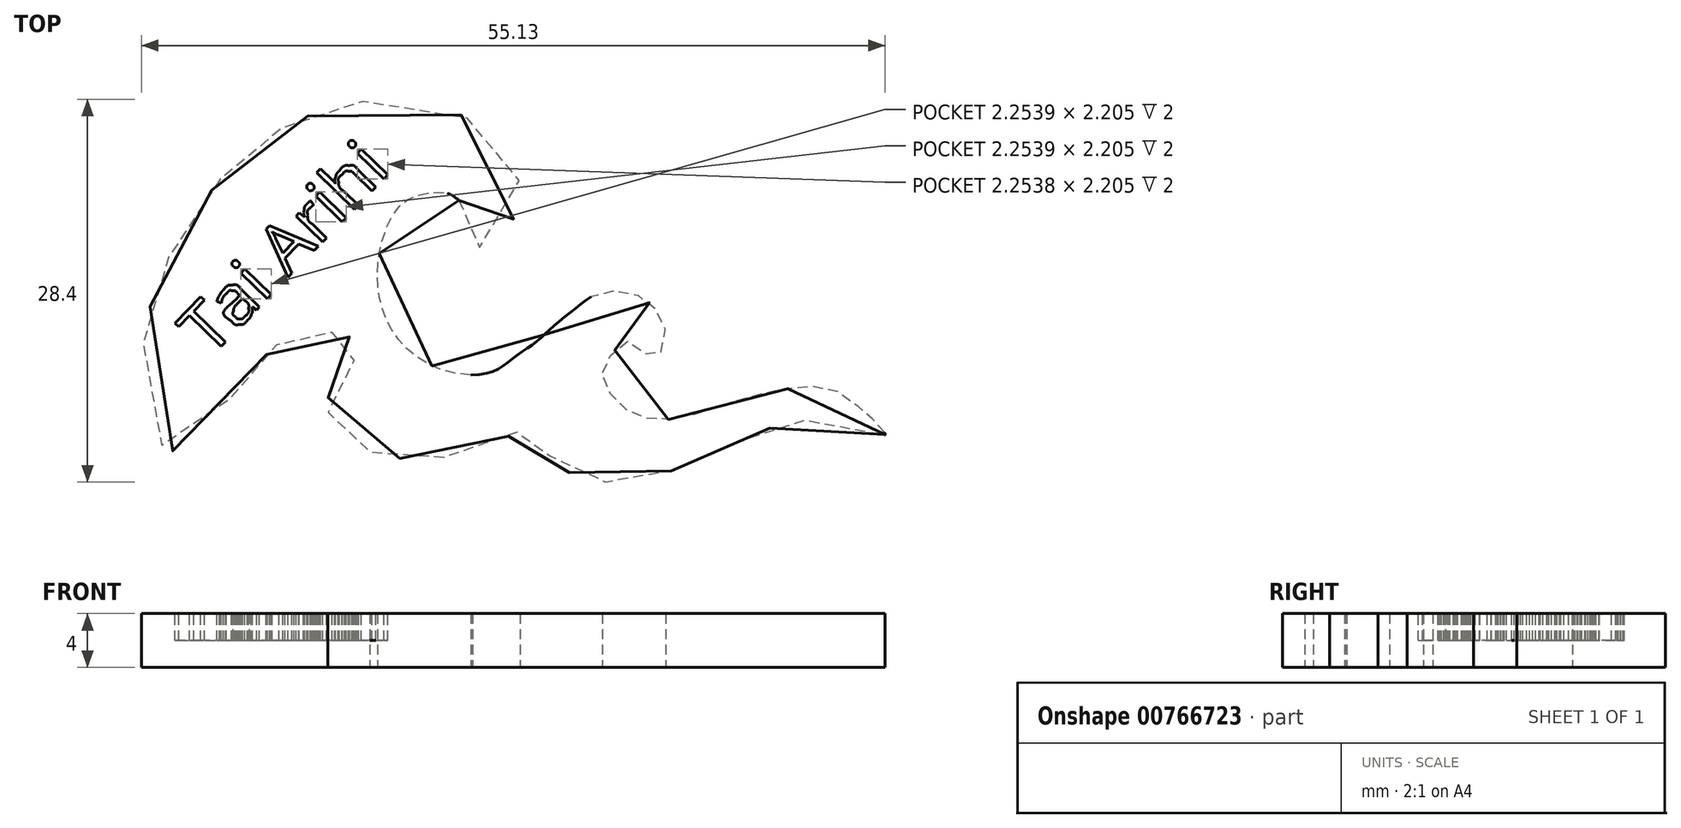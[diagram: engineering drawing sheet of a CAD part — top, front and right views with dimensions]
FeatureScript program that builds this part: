
annotation { "Feature Type Name" : "Feature", "Feature Type Description" : "" }
export const myFeature = defineFeature(function(context is Context, id is Id, definition is map)
    precondition{}
    {
        {
            var Q0;
            Q0=qCreatedBy(makeId("Top.planeOp"),FACE);
            var sketch = newSketch(context, id + "F0", { "sketchPlane" : qUnion([Q0])});
            skFitSpline(sketch, "E0", {"points": [v(-4, 7.32) * mm, v(-3.17, 6.5) * mm, v(-3.03, 5.12) * mm, v(-2.94, 3.88) * mm, v(-1.05, 4.57) * mm, v(0.33, 6.63) * mm, v(0.33, 9.3) * mm, v(-1.1, 11.33) * mm, v(-2.75, 13.03) * mm, v(-6.71, 14.6) * mm, v(-10.83, 14.7) * mm, v(-14.26, 13.9) * mm, v(-16.5, 13.04) * mm, v(-17.87, 12.21) * mm, v(-19.38, 11.18) * mm, v(-21.73, 8.83) * mm, v(-23.82, 6) * mm, v(-25.4, 3.36) * mm, v(-26.4, 0.65) * mm, v(-27.01, -0.9) * mm, v(-27.41, -7.48) * mm, v(-26.41, -10.04) * mm, v(-25.48, -11.27) * mm, v(-22.14, -9.08) * mm, v(-20.52, -6.72) * mm, v(-19, -4.9) * mm, v(-17.96, -3.83) * mm, v(-17.16, -3.15) * mm, v(-16.24, -2.8) * mm, v(-15.12, -2.5) * mm, v(-13.56, -2.45) * mm, v(-12.02, -2.86) * mm, v(-10.62, -4.24) * mm, v(-11.44, -4.4) * mm, v(-12.26, -5) * mm, v(-13.12, -5.94) * mm, v(-13.62, -6.85) * mm, v(-13.57, -8.97) * mm, v(-12.9, -10.01) * mm, v(-12.3, -10.65) * mm, v(-10.6, -11.34) * mm, v(-8, -11.86) * mm, v(-6.26, -11.88) * mm, v(-4.58, -11.65) * mm, v(-2.42, -11.25) * mm, v(-0.35, -10.18) * mm, v(1.58, -9.17) * mm, v(2, -8.82) * mm, v(2.24, -10.21) * mm, v(3.33, -12.42) * mm, v(4.27, -12.9) * mm, v(5.5, -13.34) * mm, v(7.56, -13.58) * mm, v(9.57, -13.4) * mm, v(11.07, -12.99) * mm, v(12.95, -12.28) * mm, v(15.2, -11.35) * mm, v(16.49, -10.68) * mm, v(17.86, -10.04) * mm, v(19.28, -9.48) * mm, v(21.13, -9.02) * mm, v(23.5, -9.09) * mm, v(26.74, -9.8) * mm, v(27.6, -10.05) * mm, v(26.97, -9.18) * mm, v(26.03, -8.38) * mm, v(24.07, -6.86) * mm, v(21.2, -6.54) * mm, v(18.35, -7.06) * mm, v(16.12, -7.7) * mm, v(14.1, -8.35) * mm, v(11.77, -8.9) * mm, v(9.35, -8.7) * mm, v(7.72, -7.6) * mm, v(6.64, -5.8) * mm, v(7.22, -4.21) * mm, v(8.76, -3.15) * mm, v(10.37, -4.33) * mm, v(11.3, -3.09) * mm, v(10.8, -1.06) * mm, v(9.3, 0.25) * mm, v(6.64, 0.5) * mm, v(4.87, -0.5) * mm, v(2.87, -2.14) * mm, v(1.58, -3.3) * mm, v(0, -4.4) * mm, v(-1.57, -5.4) * mm, v(-5, -5.34) * mm, v(-8.07, -3.46) * mm, v(-9.55, -1.09) * mm, v(-10.04, 1.33) * mm, v(-9.8, 3.94) * mm, v(-8.5, 6.8) * mm, v(-6.73, 7.79) * mm, v(-4.84, 7.84) * mm, v(-4, 7.32) * mm]});
            skSolve(sketch);
        }
        {
            var Q0;
            Q0 = qSketchRegion(id + "F0", true);
            extrude(context, id + "F1", {"entities" : qUnion([Q0]), "depth" : 4 * mm, "offsetDistance" : 25 * mm});
        }
        {
            var Q0;
            Q0=makeQuery(id+"F1.opExtrude","CAP_FACE",FACE,{"disambiguationData":[OSD([sQuery(id+"F0.wireOp",EDGE,"E0")])],"isStart":false});
            var sketch = newSketch(context, id + "F2", { "sketchPlane" : qUnion([Q0])});
            skLineSegment(sketch, "E1.0.0", {"start": v(-19, -0.8) * mm, "end": v(-18.79, -0.58) * mm});
            skLineSegment(sketch, "E1.0.1", {"start": v(-18.79, -0.58) * mm, "end": v(-20.13, 0.72) * mm});
            skFitSpline(sketch, "E1.0.2", {"points": [v(-20.13, 0.72) * mm, v(-20.47, 1.05) * mm, v(-20.8, 1.04) * mm]});
            skFitSpline(sketch, "E1.0.3", {"points": [v(-20.8, 1.04) * mm, v(-21.11, 1.02) * mm, v(-21.45, 0.67) * mm]});
            skFitSpline(sketch, "E1.0.4", {"points": [v(-21.45, 0.67) * mm, v(-21.62, 0.5) * mm, v(-21.75, 0.27) * mm]});
            skFitSpline(sketch, "E1.0.5", {"points": [v(-21.75, 0.27) * mm, v(-21.87, 0.06) * mm, v(-21.93, -0.16) * mm]});
            skLineSegment(sketch, "E1.0.6", {"start": v(-21.93, -0.16) * mm, "end": v(-21.62, -0.3) * mm});
            skFitSpline(sketch, "E1.0.7", {"points": [v(-21.62, -0.3) * mm, v(-21.47, 0.16) * mm, v(-21.23, 0.4) * mm]});
            skFitSpline(sketch, "E1.0.8", {"points": [v(-21.23, 0.4) * mm, v(-21.01, 0.63) * mm, v(-20.8, 0.62) * mm]});
            skFitSpline(sketch, "E1.0.9", {"points": [v(-20.8, 0.62) * mm, v(-20.6, 0.61) * mm, v(-20.37, 0.39) * mm]});
            skLineSegment(sketch, "E1.0.10", {"start": v(-20.37, 0.39) * mm, "end": v(-20.25, 0.27) * mm});
            skLineSegment(sketch, "E1.0.11", {"start": v(-20.25, 0.27) * mm, "end": v(-20.56, -0.07) * mm});
            skFitSpline(sketch, "E1.0.12", {"points": [v(-20.56, -0.07) * mm, v(-21.46, -1.05) * mm, v(-20.86, -1.63) * mm]});
            skFitSpline(sketch, "E1.0.13", {"points": [v(-20.86, -1.63) * mm, v(-20.58, -1.9) * mm, v(-20.27, -1.88) * mm]});
            skFitSpline(sketch, "E1.0.14", {"points": [v(-20.27, -1.88) * mm, v(-19.96, -1.86) * mm, v(-19.68, -1.57) * mm]});
            skFitSpline(sketch, "E1.0.15", {"points": [v(-19.68, -1.57) * mm, v(-19.46, -1.35) * mm, v(-19.39, -1.14) * mm]});
            skFitSpline(sketch, "E1.0.16", {"points": [v(-19.39, -1.14) * mm, v(-19.31, -0.93) * mm, v(-19.35, -0.6) * mm]});
            skLineSegment(sketch, "E1.0.17", {"start": v(-19.35, -0.6) * mm, "end": v(-19.34, -0.6) * mm});
            skLineSegment(sketch, "E1.0.18", {"start": v(-19.34, -0.6) * mm, "end": v(-19, -0.8) * mm});
            skLineSegment(sketch, "E2.0.0", {"start": v(-21.32, -3.2) * mm, "end": v(-23.67, -0.91) * mm});
            skLineSegment(sketch, "E2.0.1", {"start": v(-23.67, -0.91) * mm, "end": v(-22.86, -0.08) * mm});
            skLineSegment(sketch, "E2.0.2", {"start": v(-22.86, -0.08) * mm, "end": v(-23.14, 0.18) * mm});
            skLineSegment(sketch, "E2.0.3", {"start": v(-23.14, 0.18) * mm, "end": v(-25.04, -1.78) * mm});
            skLineSegment(sketch, "E2.0.4", {"start": v(-25.04, -1.78) * mm, "end": v(-24.77, -2.04) * mm});
            skLineSegment(sketch, "E2.0.5", {"start": v(-24.77, -2.04) * mm, "end": v(-23.97, -1.21) * mm});
            skLineSegment(sketch, "E2.0.6", {"start": v(-23.97, -1.21) * mm, "end": v(-21.62, -3.5) * mm});
            skLineSegment(sketch, "E2.0.7", {"start": v(-21.62, -3.5) * mm, "end": v(-21.32, -3.2) * mm});
            skFitSpline(sketch, "E3.0.0", {"points": [v(-20.71, 2.43) * mm, v(-20.61, 2.33) * mm, v(-20.52, 2.33) * mm]});
            skFitSpline(sketch, "E3.0.1", {"points": [v(-20.52, 2.33) * mm, v(-20.42, 2.34) * mm, v(-20.34, 2.41) * mm]});
            skFitSpline(sketch, "E3.0.2", {"points": [v(-20.34, 2.41) * mm, v(-20.28, 2.48) * mm, v(-20.27, 2.58) * mm]});
            skFitSpline(sketch, "E3.0.3", {"points": [v(-20.27, 2.58) * mm, v(-20.27, 2.68) * mm, v(-20.37, 2.78) * mm]});
            skFitSpline(sketch, "E3.0.4", {"points": [v(-20.37, 2.78) * mm, v(-20.47, 2.88) * mm, v(-20.57, 2.87) * mm]});
            skFitSpline(sketch, "E3.0.5", {"points": [v(-20.57, 2.87) * mm, v(-20.67, 2.87) * mm, v(-20.74, 2.8) * mm]});
            skFitSpline(sketch, "E3.0.6", {"points": [v(-20.74, 2.8) * mm, v(-20.81, 2.72) * mm, v(-20.82, 2.62) * mm]});
            skFitSpline(sketch, "E3.0.7", {"points": [v(-20.82, 2.62) * mm, v(-20.82, 2.53) * mm, v(-20.71, 2.43) * mm]});
            skLineSegment(sketch, "E4.0.0", {"start": v(-17.9, 0.33) * mm, "end": v(-19.87, 2.24) * mm});
            skLineSegment(sketch, "E4.0.1", {"start": v(-19.87, 2.24) * mm, "end": v(-20.16, 1.94) * mm});
            skLineSegment(sketch, "E4.0.2", {"start": v(-20.16, 1.94) * mm, "end": v(-18.2, 0.03) * mm});
            skLineSegment(sketch, "E4.0.3", {"start": v(-18.2, 0.03) * mm, "end": v(-17.9, 0.33) * mm});
            skLineSegment(sketch, "E5.0.0", {"start": v(-14.72, 3.6) * mm, "end": v(-14.42, 3.92) * mm});
            skLineSegment(sketch, "E5.0.1", {"start": v(-14.42, 3.92) * mm, "end": v(-18.05, 5.44) * mm});
            skLineSegment(sketch, "E5.0.2", {"start": v(-18.05, 5.44) * mm, "end": v(-18.3, 5.19) * mm});
            skLineSegment(sketch, "E5.0.3", {"start": v(-18.3, 5.19) * mm, "end": v(-16.67, 1.6) * mm});
            skLineSegment(sketch, "E5.0.4", {"start": v(-16.67, 1.6) * mm, "end": v(-16.37, 1.9) * mm});
            skLineSegment(sketch, "E5.0.5", {"start": v(-16.37, 1.9) * mm, "end": v(-16.9, 3.04) * mm});
            skLineSegment(sketch, "E5.0.6", {"start": v(-16.9, 3.04) * mm, "end": v(-15.87, 4.09) * mm});
            skLineSegment(sketch, "E5.0.7", {"start": v(-15.87, 4.09) * mm, "end": v(-14.72, 3.6) * mm});
            skFitSpline(sketch, "E6.0.0", {"points": [v(-15.24, 7.08) * mm, v(-15.42, 6.9) * mm, v(-15.47, 6.64) * mm]});
            skFitSpline(sketch, "E6.0.1", {"points": [v(-15.47, 6.64) * mm, v(-15.51, 6.38) * mm, v(-15.43, 6.08) * mm]});
            skLineSegment(sketch, "E6.0.2", {"start": v(-15.43, 6.08) * mm, "end": v(-15.44, 6.07) * mm});
            skLineSegment(sketch, "E6.0.3", {"start": v(-15.44, 6.07) * mm, "end": v(-15.84, 6.39) * mm});
            skLineSegment(sketch, "E6.0.4", {"start": v(-15.84, 6.39) * mm, "end": v(-16.07, 6.14) * mm});
            skLineSegment(sketch, "E6.0.5", {"start": v(-16.07, 6.14) * mm, "end": v(-14.11, 4.24) * mm});
            skLineSegment(sketch, "E6.0.6", {"start": v(-14.11, 4.24) * mm, "end": v(-13.82, 4.53) * mm});
            skLineSegment(sketch, "E6.0.7", {"start": v(-13.82, 4.53) * mm, "end": v(-14.88, 5.56) * mm});
            skFitSpline(sketch, "E6.0.8", {"points": [v(-14.88, 5.56) * mm, v(-15.16, 5.84) * mm, v(-15.2, 6.2) * mm]});
            skFitSpline(sketch, "E6.0.9", {"points": [v(-15.2, 6.2) * mm, v(-15.22, 6.55) * mm, v(-15, 6.8) * mm]});
            skFitSpline(sketch, "E6.0.10", {"points": [v(-15, 6.8) * mm, v(-14.9, 6.88) * mm, v(-14.76, 6.98) * mm]});
            skLineSegment(sketch, "E6.0.11", {"start": v(-14.76, 6.98) * mm, "end": v(-15, 7.29) * mm});
            skFitSpline(sketch, "E6.0.12", {"points": [v(-15, 7.29) * mm, v(-15.11, 7.2) * mm, v(-15.24, 7.08) * mm]});
            skLineSegment(sketch, "E7.0.0", {"start": v(-12.37, 6.03) * mm, "end": v(-14.33, 7.94) * mm});
            skLineSegment(sketch, "E7.0.1", {"start": v(-14.33, 7.94) * mm, "end": v(-14.62, 7.64) * mm});
            skLineSegment(sketch, "E7.0.2", {"start": v(-14.62, 7.64) * mm, "end": v(-12.66, 5.74) * mm});
            skLineSegment(sketch, "E7.0.3", {"start": v(-12.66, 5.74) * mm, "end": v(-12.37, 6.03) * mm});
            skFitSpline(sketch, "E8.0.0", {"points": [v(-15.18, 8.13) * mm, v(-15.08, 8.04) * mm, v(-14.98, 8.04) * mm]});
            skFitSpline(sketch, "E8.0.1", {"points": [v(-14.98, 8.04) * mm, v(-14.88, 8.04) * mm, v(-14.8, 8.12) * mm]});
            skFitSpline(sketch, "E8.0.2", {"points": [v(-14.8, 8.12) * mm, v(-14.74, 8.19) * mm, v(-14.74, 8.29) * mm]});
            skFitSpline(sketch, "E8.0.3", {"points": [v(-14.74, 8.29) * mm, v(-14.74, 8.39) * mm, v(-14.84, 8.49) * mm]});
            skFitSpline(sketch, "E8.0.4", {"points": [v(-14.84, 8.49) * mm, v(-14.94, 8.58) * mm, v(-15.03, 8.58) * mm]});
            skFitSpline(sketch, "E8.0.5", {"points": [v(-15.03, 8.58) * mm, v(-15.13, 8.57) * mm, v(-15.2, 8.5) * mm]});
            skFitSpline(sketch, "E8.0.6", {"points": [v(-15.2, 8.5) * mm, v(-15.28, 8.43) * mm, v(-15.28, 8.33) * mm]});
            skFitSpline(sketch, "E8.0.7", {"points": [v(-15.28, 8.33) * mm, v(-15.28, 8.23) * mm, v(-15.18, 8.13) * mm]});
            skLineSegment(sketch, "E9.0.0", {"start": v(-10.45, 8) * mm, "end": v(-10.16, 8.3) * mm});
            skLineSegment(sketch, "E9.0.1", {"start": v(-10.16, 8.3) * mm, "end": v(-11.44, 9.55) * mm});
            skFitSpline(sketch, "E9.0.2", {"points": [v(-11.44, 9.55) * mm, v(-11.81, 9.91) * mm, v(-12.16, 9.9) * mm]});
            skFitSpline(sketch, "E9.0.3", {"points": [v(-12.16, 9.9) * mm, v(-12.5, 9.88) * mm, v(-12.86, 9.52) * mm]});
            skFitSpline(sketch, "E9.0.4", {"points": [v(-12.86, 9.52) * mm, v(-13.06, 9.32) * mm, v(-13.13, 9.07) * mm]});
            skFitSpline(sketch, "E9.0.5", {"points": [v(-13.13, 9.07) * mm, v(-13.2, 8.83) * mm, v(-13.15, 8.6) * mm]});
            skLineSegment(sketch, "E9.0.6", {"start": v(-13.15, 8.6) * mm, "end": v(-13.17, 8.6) * mm});
            skFitSpline(sketch, "E9.0.7", {"points": [v(-13.17, 8.6) * mm, v(-13.26, 8.7) * mm, v(-13.4, 8.85) * mm]});
            skLineSegment(sketch, "E9.0.8", {"start": v(-13.4, 8.85) * mm, "end": v(-14.25, 9.67) * mm});
            skLineSegment(sketch, "E9.0.9", {"start": v(-14.25, 9.67) * mm, "end": v(-14.54, 9.37) * mm});
            skLineSegment(sketch, "E9.0.10", {"start": v(-14.54, 9.37) * mm, "end": v(-11.75, 6.66) * mm});
            skLineSegment(sketch, "E9.0.11", {"start": v(-11.75, 6.66) * mm, "end": v(-11.46, 6.96) * mm});
            skLineSegment(sketch, "E9.0.12", {"start": v(-11.46, 6.96) * mm, "end": v(-12.5, 7.96) * mm});
            skFitSpline(sketch, "E9.0.13", {"points": [v(-12.5, 7.96) * mm, v(-12.88, 8.33) * mm, v(-12.9, 8.64) * mm]});
            skFitSpline(sketch, "E9.0.14", {"points": [v(-12.9, 8.64) * mm, v(-12.94, 8.94) * mm, v(-12.64, 9.25) * mm]});
            skFitSpline(sketch, "E9.0.15", {"points": [v(-12.64, 9.25) * mm, v(-12.4, 9.49) * mm, v(-12.18, 9.48) * mm]});
            skFitSpline(sketch, "E9.0.16", {"points": [v(-12.18, 9.48) * mm, v(-11.96, 9.48) * mm, v(-11.72, 9.24) * mm]});
            skLineSegment(sketch, "E9.0.17", {"start": v(-11.72, 9.24) * mm, "end": v(-10.45, 8) * mm});
            skFitSpline(sketch, "E10.0.0", {"points": [v(-12.09, 11.32) * mm, v(-11.99, 11.22) * mm, v(-11.89, 11.22) * mm]});
            skFitSpline(sketch, "E10.0.1", {"points": [v(-11.89, 11.22) * mm, v(-11.8, 11.22) * mm, v(-11.72, 11.3) * mm]});
            skFitSpline(sketch, "E10.0.2", {"points": [v(-11.72, 11.3) * mm, v(-11.65, 11.37) * mm, v(-11.65, 11.47) * mm]});
            skFitSpline(sketch, "E10.0.3", {"points": [v(-11.65, 11.47) * mm, v(-11.65, 11.57) * mm, v(-11.75, 11.67) * mm]});
            skFitSpline(sketch, "E10.0.4", {"points": [v(-11.75, 11.67) * mm, v(-11.85, 11.77) * mm, v(-11.95, 11.76) * mm]});
            skFitSpline(sketch, "E10.0.5", {"points": [v(-11.95, 11.76) * mm, v(-12.04, 11.76) * mm, v(-12.11, 11.68) * mm]});
            skFitSpline(sketch, "E10.0.6", {"points": [v(-12.11, 11.68) * mm, v(-12.19, 11.6) * mm, v(-12.19, 11.51) * mm]});
            skFitSpline(sketch, "E10.0.7", {"points": [v(-12.19, 11.51) * mm, v(-12.2, 11.42) * mm, v(-12.09, 11.32) * mm]});
            skLineSegment(sketch, "E11.0.0", {"start": v(-9.28, 9.22) * mm, "end": v(-11.24, 11.12) * mm});
            skLineSegment(sketch, "E11.0.1", {"start": v(-11.24, 11.12) * mm, "end": v(-11.53, 10.82) * mm});
            skLineSegment(sketch, "E11.0.2", {"start": v(-11.53, 10.82) * mm, "end": v(-9.57, 8.92) * mm});
            skLineSegment(sketch, "E11.0.3", {"start": v(-9.57, 8.92) * mm, "end": v(-9.28, 9.22) * mm});
            skLineSegment(sketch, "E12.0.0", {"start": v(-17.58, 4.5) * mm, "end": v(-17.06, 3.41) * mm});
            skLineSegment(sketch, "E12.0.1", {"start": v(-17.06, 3.41) * mm, "end": v(-16.24, 4.26) * mm});
            skLineSegment(sketch, "E12.0.2", {"start": v(-16.24, 4.26) * mm, "end": v(-17.35, 4.74) * mm});
            skFitSpline(sketch, "E12.0.3", {"points": [v(-17.35, 4.74) * mm, v(-17.56, 4.83) * mm, v(-17.84, 4.99) * mm]});
            skFitSpline(sketch, "E12.0.4", {"points": [v(-17.84, 4.99) * mm, v(-17.71, 4.78) * mm, v(-17.58, 4.5) * mm]});
            skFitSpline(sketch, "E13.0.0", {"points": [v(-20.55, -1.32) * mm, v(-20.4, -1.48) * mm, v(-20.21, -1.46) * mm]});
            skFitSpline(sketch, "E13.0.1", {"points": [v(-20.21, -1.46) * mm, v(-20.04, -1.45) * mm, v(-19.86, -1.27) * mm]});
            skFitSpline(sketch, "E13.0.2", {"points": [v(-19.86, -1.27) * mm, v(-19.6, -1) * mm, v(-19.6, -0.69) * mm]});
            skFitSpline(sketch, "E13.0.3", {"points": [v(-19.6, -0.69) * mm, v(-19.6, -0.38) * mm, v(-19.87, -0.11) * mm]});
            skLineSegment(sketch, "E13.0.4", {"start": v(-19.87, -0.11) * mm, "end": v(-20.04, 0.06) * mm});
            skLineSegment(sketch, "E13.0.5", {"start": v(-20.04, 0.06) * mm, "end": v(-20.32, -0.25) * mm});
            skFitSpline(sketch, "E13.0.6", {"points": [v(-20.32, -0.25) * mm, v(-20.65, -0.62) * mm, v(-20.7, -0.87) * mm]});
            skFitSpline(sketch, "E13.0.7", {"points": [v(-20.7, -0.87) * mm, v(-20.76, -1.12) * mm, v(-20.55, -1.32) * mm]});
            skSolve(sketch);
        }
        {
            var Q0;
            Q0 = qSketchRegion(id + "F2", true);
            extrude(context, id + "F3", {"entities" : qUnion([Q0]), "operationType" : NewBodyOperationType.REMOVE, "oppositeDirection" : true, "depth" : 2 * mm, "offsetDistance" : 25 * mm});
        }
    });
